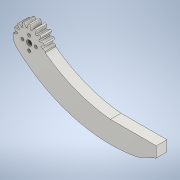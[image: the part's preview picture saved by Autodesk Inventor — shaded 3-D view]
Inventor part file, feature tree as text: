
AUTODESK INVENTOR PART (.ipt)
format: ipt  version: 2020 (Build 240168000, 168)  size: 365,568 bytes
history: native  units: mm (DEFAULTED — no unit token found)
features: sketch x14, extrude x13, plane x3, other x3
ambient origin geometry x8: Origin, YZ Plane, XZ Plane, XY Plane, X Axis, Y Axis, Z Axis, Center Point
bodies: Solid1 (feature_tree)
feature tree (33):
  extrude  "Extrusion1"  Depth=12.7mm TaperAngle=0.0deg
  plane  "Work Plane1"
  plane  "Work Plane2"
  plane  "Work Plane3"
  other  "Spur Gear"
  extrude  "Extrusion2"  Depth=76.2mm TaperAngle=0.0deg
  sketch  "Sketch4"  dims[d14=0.0mm d15=34.076615mm]
  extrude  "Extrusion3"  TaperAngle=0.0deg  [1 undecoded]
  extrude  "Extrusion4"  Depth=34.076615mm
  extrude  "Extrusion5"  TaperAngle=0.0deg  [1 undecoded]
  extrude  "Extrusion6"  Depth=34.076615mm
  extrude  "Extrusion7"  Depth=31.6611mm
  extrude  "Extrusion9"  Depth=12.7mm TaperAngle=0.0deg
  extrude  "Extrusion10"  Depth=12.7mm
  extrude  "Extrusion11"  Depth=12.7mm
  extrude  "Extrusion13"  Depth=12.7mm TaperAngle=0.0deg
  extrude  "Extrusion15"  Depth=12.7mm TaperAngle=0.0deg
  extrude  "Extrusion16"  Depth=12.7mm TaperAngle=0.0deg
  sketch  "Sketch1"  dims[d0=38.305046mm d1=12.7mm d2=0.0mm]
  sketch  "Sketch2"  dims[d3=34.076615mm d4=76.2mm d5=0.0mm]
  other  "Srf1"
  sketch  "Sketch3"  dims[d6=0.0mm d7=1.963495mm d9=0.0mm]
  sketch  "Sketch6"  dims[d16=0.0mm d17=0.0mm]
  sketch  "Sketch7"  dims[d18=0.0mm d19=34.076615mm]
  sketch  "Sketch8"  dims[d25=25.4mm d26=0.0mm d27=31.6611mm]
  sketch  "Sketch9"  dims[d28=127.0mm d29=12.7mm d30=0.0mm]
  sketch  "Sketch11"  dims[d31=12.7mm d32=0.0mm d33=38.1mm]
  sketch  "Sketch12"  dims[d34=12.7mm d35=25.4mm]
  sketch  "Sketch13"  dims[d36=12.7mm d37=0.0mm d38=12.7mm d39=0.0mm]
  sketch  "Sketch15"  dims[d40=12.7mm d41=0.0mm d48=12.7mm d49=0.0mm]
  sketch  "Sketch17"  dims[d50=12.7mm d51=0.0mm d52=12.7mm d53=0.0mm]
  sketch  "Sketch18"  dims[d60=12.7mm d61=0.0mm d65=12.7mm d66=0.0mm d67=16.002mm d68=3.5814mm d69=3.5814mm d70=3.5814mm d71=3.5814mm d72=6.35mm d73=57.15mm d74=0.0mm d24=12.7mm]
  other  "Pitch Diameter"
note: 2 required parameter values undecoded (feature->parameter linkage not recoverable at this tier; creation-order binding heuristic only, values carry confidence <= 0.55)
